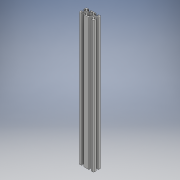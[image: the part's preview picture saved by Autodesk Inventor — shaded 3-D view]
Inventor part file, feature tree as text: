
AUTODESK INVENTOR PART (.ipt)
format: ipt  version: 2018 (Build 220112000, 112)  size: 342,528 bytes
history: native  units: mm
features: extrude x1, sketch x1, projected_geometry x1, imported_body x1
ambient origin geometry x8: Origin, YZ Plane, XZ Plane, XY Plane, X Axis, Y Axis, Z Axis, Center Point
bodies: Solid1 (feature_tree)
feature tree (4):
  extrude  "Extrusion1"  [1 undecoded]
  sketch  "Sketch1"  dims[d0=640.0mm d1=0.0mm]
  projected_geometry  "Projected Loop1"
  imported_body  "Base1"
note: 1 required parameter value undecoded (feature->parameter linkage not recoverable at this tier; creation-order binding heuristic only, values carry confidence <= 0.55)
